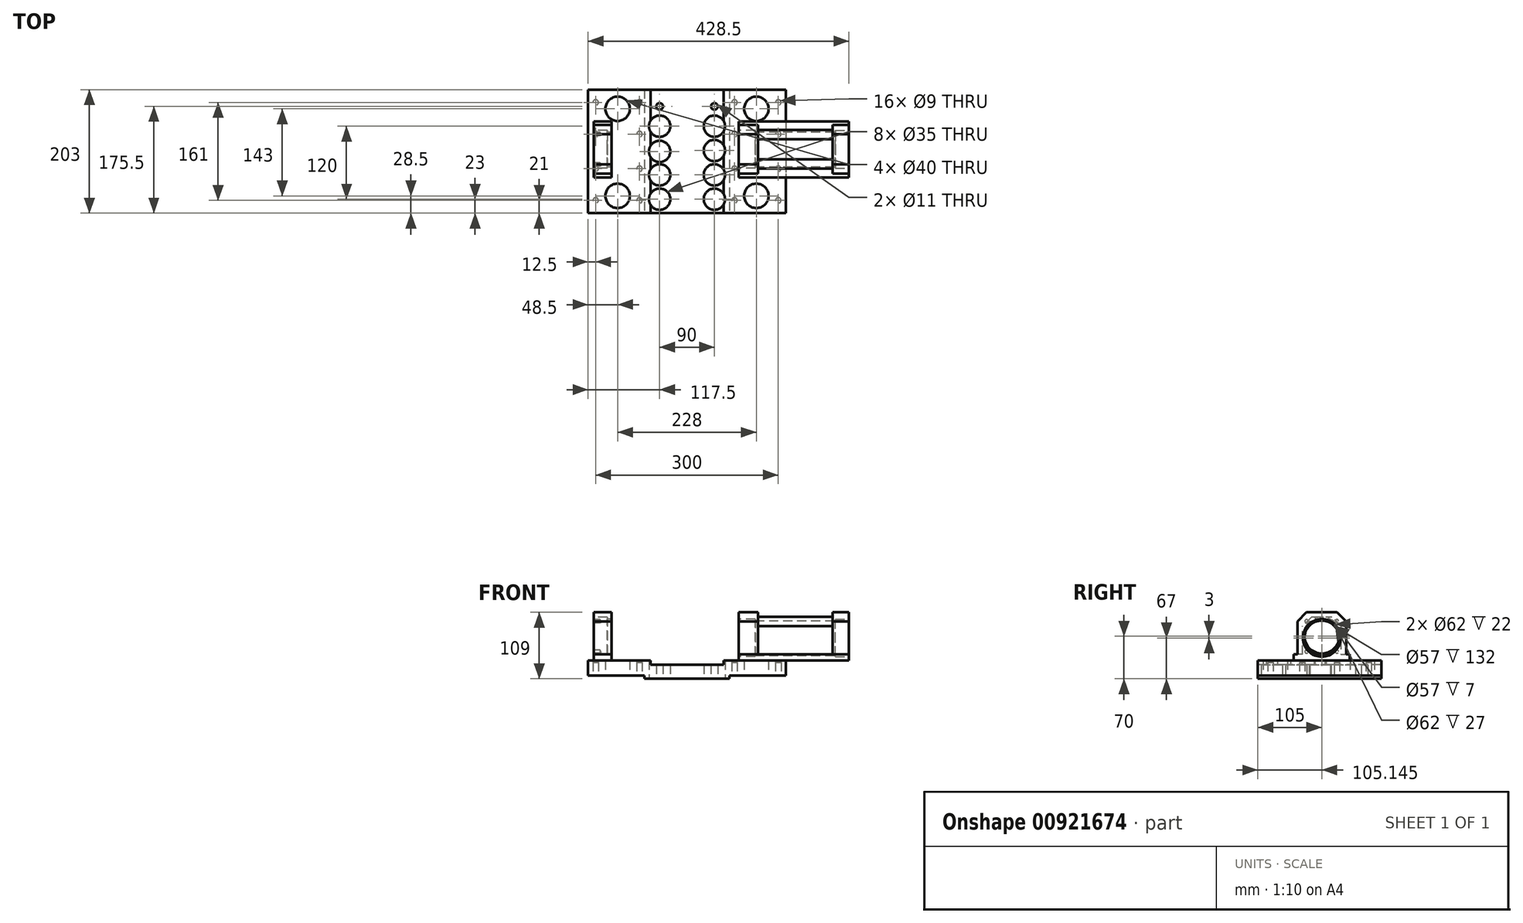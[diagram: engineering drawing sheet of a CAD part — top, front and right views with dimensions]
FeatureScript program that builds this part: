
annotation { "Feature Type Name" : "Feature", "Feature Type Description" : "" }
export const myFeature = defineFeature(function(context is Context, id is Id, definition is map)
    precondition{}
    {
        {
            var Q0;
            Q0=qCreatedBy(makeId("Front.planeOp"),FACE);
            var sketch = newSketch(context, id + "F0", { "sketchPlane" : qUnion([Q0])});
            skLineSegment(sketch, "E0", {"start": v(0, 0) * mm, "end": v(0, 25) * mm});
            skLineSegment(sketch, "E1", {"start": v(0, 25) * mm, "end": v(325, 25) * mm});
            skLineSegment(sketch, "E2", {"start": v(325, 25) * mm, "end": v(325, 0) * mm});
            skLineSegment(sketch, "E3", {"start": v(325, 0) * mm, "end": v(232.5, 0) * mm});
            skLineSegment(sketch, "E4", {"start": v(232.5, 0) * mm, "end": v(232.5, -5) * mm});
            skLineSegment(sketch, "E5", {"start": v(232.5, -5) * mm, "end": v(92.5, -5) * mm});
            skLineSegment(sketch, "E6", {"start": v(92.5, -5) * mm, "end": v(92.5, 0) * mm});
            skLineSegment(sketch, "E7", {"start": v(92.5, 0) * mm, "end": v(0, 0) * mm});
            skLineSegment(sketch, "E8", {"start": v(162.5, 25) * mm, "end": v(162.5, -5) * mm, "construction": true});
            skLineSegment(sketch, "E9", {"start": v(102.5, 25) * mm, "end": v(102.5, 18) * mm});
            skLineSegment(sketch, "E10", {"start": v(102.5, 18) * mm, "end": v(222.5, 18) * mm});
            skLineSegment(sketch, "E11", {"start": v(222.5, 18) * mm, "end": v(222.5, 25) * mm});
            skLineSegment(sketch, "E12", {"start": v(102.5, 25) * mm, "end": v(222.5, 25) * mm});
            skSolve(sketch);
        }
        {
            var Q0;
            {var subQ1=sQuery(id+"F0.wireOp",EDGE,"E0");Q0=makeQuery(id+"F0.imprint","IMPRINT",FACE,{"disambiguationData":[TD([[makeQuery(id+"F0.imprint","IMPRINT",EDGE,{"derivedFrom":subQ1}),-1.0]])]});}
            extrude(context, id + "F1", {"entities" : qUnion([Q0]), "oppositeDirection" : true, "depth" : 203 * mm, "offsetDistance" : 25 * mm});
        }
        {
            var Q0;
            Q0=qCreatedBy(makeId("Right.planeOp"),FACE);
            cPlane(context, id + "F2", {"entities" : qUnion([Q0]), "cplaneType" : CPlaneType.OFFSET, "offset" : 38.5 * mm, "width" : 150 * mm, "height" : 150 * mm});
        }
        {
            var Q0;
            Q0=qCreatedBy(id+"F2.planeOp",FACE);
            var sketch = newSketch(context, id + "F3", { "sketchPlane" : qUnion([Q0])});
            skLineSegment(sketch, "E13.0", {"start": v(203, 25) * mm, "end": v(0, 25) * mm});
            skPoint(sketch, "E14", {"position": v(105, 25) * mm});
            skLineSegment(sketch, "E15", {"start": v(105, 114.48) * mm, "end": v(105, -54.55) * mm, "construction": true});
            skLineSegment(sketch, "E16", {"start": v(59, 25) * mm, "end": v(59, 35) * mm});
            skLineSegment(sketch, "E17", {"start": v(59, 35) * mm, "end": v(65, 35) * mm});
            skLineSegment(sketch, "E18", {"start": v(65, 35) * mm, "end": v(65, 104) * mm});
            skLineSegment(sketch, "E19", {"start": v(65, 104) * mm, "end": v(145, 104) * mm});
            skLineSegment(sketch, "E20", {"start": v(145, 104) * mm, "end": v(145, 35) * mm});
            skLineSegment(sketch, "E21", {"start": v(145, 35) * mm, "end": v(151, 35) * mm});
            skLineSegment(sketch, "E22", {"start": v(151, 35) * mm, "end": v(151, 25) * mm});
            skLineSegment(sketch, "E23", {"start": v(151, 25) * mm, "end": v(59, 25) * mm});
            skLineSegment(sketch, "E24", {"start": v(65, 69.5) * mm, "end": v(145, 69.5) * mm, "construction": true});
            skSolve(sketch);
        }
        {
            var Q0;
            {var subQ0=sQuery(id+"F3.wireOp",EDGE,"E16");Q0=makeQuery(id+"F3.imprint","IMPRINT",FACE,{"disambiguationData":[TD([[makeQuery(id+"F3.imprint","IMPRINT",EDGE,{"derivedFrom":subQ0}),-1.0]])]});}
            extrude(context, id + "F4", {"entities" : qUnion([Q0]), "operationType" : NewBodyOperationType.ADD, "oppositeDirection" : true, "depth" : 29 * mm, "offsetDistance" : 25 * mm});
        }
        {
            var Q0;
            Q0=makeQuery(id+"F4.opExtrude","SWEPT_EDGE",EDGE,{"disambiguationData":[OSD([sQuery(id+"F3.wireOp",EDGE,"E18"),sQuery(id+"F3.wireOp",EDGE,"E19")])]});
            var Q1;
            Q1=makeQuery(id+"F4.opExtrude","SWEPT_EDGE",EDGE,{"disambiguationData":[OSD([sQuery(id+"F3.wireOp",EDGE,"E19"),sQuery(id+"F3.wireOp",EDGE,"E20")])]});
            chamfer(context, id + "F5", {"entities" : qUnion([Q0, Q1]), "width" : 15 * mm, "tangentPropagation" : true});
        }
        {
            var Q0;
            Q0=makeQuery(id+"F4.opExtrude","CAP_FACE",FACE,{"disambiguationData":[OSD([sQuery(id+"F3.wireOp",EDGE,"E13.0"),sQuery(id+"F3.wireOp",EDGE,"E16"),sQuery(id+"F3.wireOp",EDGE,"E17"),sQuery(id+"F3.wireOp",EDGE,"E18"),sQuery(id+"F3.wireOp",EDGE,"E19"),sQuery(id+"F3.wireOp",EDGE,"E20"),sQuery(id+"F3.wireOp",EDGE,"E21"),sQuery(id+"F3.wireOp",EDGE,"E22")])],"isStart":true});
            var sketch = newSketch(context, id + "F6", { "sketchPlane" : qUnion([Q0])});
            skPoint(sketch, "E25", {"position": v(105.15, 65) * mm});
            skCircle(sketch, "E26", {"center": v(105.15, 65) * mm, "radius": 28.5 * mm});
            skSolve(sketch);
        }
        {
            var Q0;
            Q0=makeQuery(id+"F6.imprint","IMPRINT",FACE,{"disambiguationData":[TD([[makeQuery(id+"F6.imprint","IMPRINT",EDGE,{"derivedFrom":sQuery(id+"F6.wireOp",EDGE,"E26")}),1.0]])]});
            extrude(context, id + "F7", {"entities" : qUnion([Q0]), "operationType" : NewBodyOperationType.REMOVE, "oppositeDirection" : true, "depth" : 7 * mm, "offsetDistance" : 25 * mm});
        }
        {
            var Q0;
            Q0=makeQuery(id+"F4.opExtrude","CAP_FACE",FACE,{"disambiguationData":[OSD([sQuery(id+"F3.wireOp",EDGE,"E13.0"),sQuery(id+"F3.wireOp",EDGE,"E16"),sQuery(id+"F3.wireOp",EDGE,"E17"),sQuery(id+"F3.wireOp",EDGE,"E18"),sQuery(id+"F3.wireOp",EDGE,"E19"),sQuery(id+"F3.wireOp",EDGE,"E20"),sQuery(id+"F3.wireOp",EDGE,"E21"),sQuery(id+"F3.wireOp",EDGE,"E22")])],"isStart":false});
            var sketch = newSketch(context, id + "F8", { "sketchPlane" : qUnion([Q0])});
            skLineSegment(sketch, "E27", {"start": v(-105, 104) * mm, "end": v(-105, 0) * mm, "construction": true});
            skPoint(sketch, "E27.endSnap0", {"position": v(-105, 25) * mm});
            skPoint(sketch, "E28", {"position": v(-105, 65) * mm});
            skCircle(sketch, "E29", {"center": v(-105, 65) * mm, "radius": 31 * mm});
            skSolve(sketch);
        }
        {
            var Q0;
            Q0=makeQuery(id+"F8.imprint","IMPRINT",FACE,{"disambiguationData":[TD([[makeQuery(id+"F8.imprint","IMPRINT",EDGE,{"derivedFrom":sQuery(id+"F8.wireOp",EDGE,"E29")}),1.0]])]});
            var Q1;
            Q1=sQuery(id+"F8.wireOp",EDGE,"E29");
            extrude(context, id + "F9", {"entities" : qUnion([Q0]), "operationType" : NewBodyOperationType.REMOVE, "surfaceEntities" : qUnion([Q1]), "oppositeDirection" : true, "depth" : 22 * mm, "offsetDistance" : 25 * mm});
        }
        {
            var Q0;
            Q0=qCreatedBy(makeId("Top.planeOp"),FACE);
            var sketch = newSketch(context, id + "F10", { "sketchPlane" : qUnion([Q0])});
            skLineSegment(sketch, "E30.0", {"start": v(0, 203) * mm, "end": v(102.5, 203) * mm, "construction": true});
            skLineSegment(sketch, "E31", {"start": v(48.5, 203) * mm, "end": v(48.5, 0) * mm, "construction": true});
            skLineSegment(sketch, "E32", {"start": v(84.5, 203) * mm, "end": v(84.5, 0) * mm, "construction": true});
            skLineSegment(sketch, "E33.0", {"start": v(102.5, 203) * mm, "end": v(222.5, 203) * mm});
            skLineSegment(sketch, "E34", {"start": v(162.5, 203) * mm, "end": v(162.5, 0) * mm, "construction": true});
            skLineSegment(sketch, "E35", {"start": v(117.5, 203) * mm, "end": v(117.5, 0) * mm, "construction": true});
            skLineSegment(sketch, "E36", {"start": v(207.5, 203) * mm, "end": v(207.5, 0) * mm, "construction": true});
            skLineSegment(sketch, "E37.0", {"start": v(222.5, 203) * mm, "end": v(325, 203) * mm, "construction": true});
            skLineSegment(sketch, "E38", {"start": v(240.5, 203) * mm, "end": v(240.5, 0) * mm, "construction": true});
            skLineSegment(sketch, "E39", {"start": v(276.5, 203) * mm, "end": v(276.5, 0) * mm, "construction": true});
            skLineSegment(sketch, "E40", {"start": v(12.5, 203) * mm, "end": v(12.5, 0) * mm, "construction": true});
            skLineSegment(sketch, "E41", {"start": v(312.5, 203) * mm, "end": v(312.5, 0) * mm, "construction": true});
            skPoint(sketch, "E42", {"position": v(12.5, 182) * mm});
            skPoint(sketch, "E43", {"position": v(12.5, 130) * mm});
            skPoint(sketch, "E44", {"position": v(12.5, 73) * mm});
            skPoint(sketch, "E45", {"position": v(12.5, 21) * mm});
            skPoint(sketch, "E46", {"position": v(48.5, 171.5) * mm});
            skPoint(sketch, "E47", {"position": v(48.5, 28.5) * mm});
            skPoint(sketch, "E48", {"position": v(84.5, 182) * mm});
            skPoint(sketch, "E49", {"position": v(84.5, 130) * mm});
            skPoint(sketch, "E50", {"position": v(84.5, 73) * mm});
            skPoint(sketch, "E51", {"position": v(84.5, 21) * mm});
            skPoint(sketch, "E52", {"position": v(117.5, 175.5) * mm});
            skPoint(sketch, "E53", {"position": v(207.5, 175.5) * mm});
            skPoint(sketch, "E54", {"position": v(117.5, 143) * mm});
            skPoint(sketch, "E55", {"position": v(117.5, 103) * mm});
            skPoint(sketch, "E56", {"position": v(117.5, 63) * mm});
            skPoint(sketch, "E57", {"position": v(117.5, 23) * mm});
            skPoint(sketch, "E58", {"position": v(207.5, 143) * mm});
            skPoint(sketch, "E59", {"position": v(207.5, 103) * mm});
            skPoint(sketch, "E60", {"position": v(207.5, 63) * mm});
            skPoint(sketch, "E61", {"position": v(207.5, 23) * mm});
            skPoint(sketch, "E62", {"position": v(240.5, 182) * mm});
            skPoint(sketch, "E63", {"position": v(240.5, 130) * mm});
            skPoint(sketch, "E64", {"position": v(240.5, 73) * mm});
            skPoint(sketch, "E65", {"position": v(240.5, 21) * mm});
            skPoint(sketch, "E66", {"position": v(312.5, 21) * mm});
            skPoint(sketch, "E67", {"position": v(312.5, 73) * mm});
            skPoint(sketch, "E68", {"position": v(312.5, 130) * mm});
            skPoint(sketch, "E69", {"position": v(312.5, 182) * mm});
            skPoint(sketch, "E70", {"position": v(276.5, 171.5) * mm});
            skPoint(sketch, "E71", {"position": v(276.5, 28.5) * mm});
            skLineSegment(sketch, "E72.0", {"start": v(0, 203) * mm, "end": v(0, 0) * mm, "construction": true});
            skPoint(sketch, "E73", {"position": v(0, 101.5) * mm});
            skLineSegment(sketch, "E74", {"start": v(0, 101.5) * mm, "end": v(351.57, 101.5) * mm, "construction": true});
            skLineSegment(sketch, "E75.0", {"start": v(102.5, 203) * mm, "end": v(102.5, 0) * mm});
            skLineSegment(sketch, "E76.0", {"start": v(222.5, 203) * mm, "end": v(222.5, 0) * mm});
            skLineSegment(sketch, "E77", {"start": v(102.5, 148) * mm, "end": v(222.5, 148) * mm});
            skSolve(sketch);
        }
        {
            var Q0;
            Q0=sQuery(id+"F10.wireOp",VERTEX,"E42");
            var Q1;
            Q1=sQuery(id+"F10.wireOp",VERTEX,"E43");
            var Q2;
            Q2=sQuery(id+"F10.wireOp",VERTEX,"E44");
            var Q3;
            Q3=sQuery(id+"F10.wireOp",VERTEX,"E45");
            var Q4;
            Q4=sQuery(id+"F10.wireOp",VERTEX,"E50");
            var Q5;
            Q5=sQuery(id+"F10.wireOp",VERTEX,"E49");
            var Q6;
            Q6=sQuery(id+"F10.wireOp",VERTEX,"E48");
            var Q7;
            Q7=sQuery(id+"F10.wireOp",VERTEX,"E62");
            var Q8;
            Q8=sQuery(id+"F10.wireOp",VERTEX,"E69");
            var Q9;
            Q9=sQuery(id+"F10.wireOp",VERTEX,"E63");
            var Q10;
            Q10=sQuery(id+"F10.wireOp",VERTEX,"E68");
            var Q11;
            Q11=sQuery(id+"F10.wireOp",VERTEX,"E64");
            var Q12;
            Q12=sQuery(id+"F10.wireOp",VERTEX,"E67");
            var Q13;
            Q13=sQuery(id+"F10.wireOp",VERTEX,"E65");
            var Q14;
            Q14=sQuery(id+"F10.wireOp",VERTEX,"E66");
            var Q15;
            Q15=sQuery(id+"F10.wireOp",VERTEX,"E51");
            var Q16;
            Q16=makeQuery(id+"F1.opExtrude","SWEPT_BODY",BODY,{"disambiguationData":[OSD([sQuery(id+"F0.wireOp",EDGE,"E0"),sQuery(id+"F0.wireOp",EDGE,"E1"),sQuery(id+"F0.wireOp",EDGE,"E2"),sQuery(id+"F0.wireOp",EDGE,"E3"),sQuery(id+"F0.wireOp",EDGE,"E4"),sQuery(id+"F0.wireOp",EDGE,"E5"),sQuery(id+"F0.wireOp",EDGE,"E6"),sQuery(id+"F0.wireOp",EDGE,"E7"),sQuery(id+"F0.wireOp",EDGE,"E9"),sQuery(id+"F0.wireOp",EDGE,"E10"),sQuery(id+"F0.wireOp",EDGE,"E11")])]});
            hole(context, id + "F11", {"style" : HoleStyle.SIMPLE, "endStyle" : HoleEndStyle.BLIND, "oppositeDirection" : true, "standardTappedOrClearance" : lookupTablePath({ "fit" : "Normal", "standard" : "ISO", "size" : "M8", "type" : "Clearance" }), "standardBlindInLast" : lookupTablePath({ "fit" : "Normal", "standard" : "ISO", "size" : "M8", "type" : "Clearance" }), "holeDiameter" : 9 * mm, "majorDiameter" : 5 * mm, "holeDepth" : 22 * mm, "isTappedThrough" : true, "tappedDepth" : 12 * mm, "tapClearance" : 3, "locations" : qUnion([Q0, Q1, Q2, Q3, Q4, Q5, Q6, Q7, Q8, Q9, Q10, Q11, Q12, Q13, Q14, Q15]), "scope" : qUnion([Q16])});
        }
        {
            var Q0;
            Q0=sQuery(id+"F10.wireOp",VERTEX,"E47");
            var Q1;
            Q1=sQuery(id+"F10.wireOp",VERTEX,"E46");
            var Q2;
            Q2=sQuery(id+"F10.wireOp",VERTEX,"E71");
            var Q3;
            Q3=sQuery(id+"F10.wireOp",VERTEX,"E70");
            var Q4;
            Q4=makeQuery(id+"F1.opExtrude","SWEPT_BODY",BODY,{"disambiguationData":[OSD([sQuery(id+"F0.wireOp",EDGE,"E0"),sQuery(id+"F0.wireOp",EDGE,"E1"),sQuery(id+"F0.wireOp",EDGE,"E2"),sQuery(id+"F0.wireOp",EDGE,"E3"),sQuery(id+"F0.wireOp",EDGE,"E4"),sQuery(id+"F0.wireOp",EDGE,"E5"),sQuery(id+"F0.wireOp",EDGE,"E6"),sQuery(id+"F0.wireOp",EDGE,"E7"),sQuery(id+"F0.wireOp",EDGE,"E9"),sQuery(id+"F0.wireOp",EDGE,"E10"),sQuery(id+"F0.wireOp",EDGE,"E11")])]});
            hole(context, id + "F12", {"style" : HoleStyle.SIMPLE, "endStyle" : HoleEndStyle.THROUGH, "oppositeDirection" : true, "holeDiameter" : 40 * mm, "majorDiameter" : 5 * mm, "isTappedThrough" : true, "tappedDepth" : 12 * mm, "tapClearance" : 3, "locations" : qUnion([Q0, Q1, Q2, Q3]), "scope" : qUnion([Q4])});
        }
        {
            var Q0;
            Q0=makeQuery(id+"F1.opExtrude","SWEPT_FACE",FACE,{"disambiguationData":[OSD([sQuery(id+"F0.wireOp",EDGE,"E5")])]});
            var sketch = newSketch(context, id + "F13", { "sketchPlane" : qUnion([Q0])});
            skPoint(sketch, "E78.0", {"position": v(117.5, -23) * mm});
            skPoint(sketch, "E79.0", {"position": v(207.5, -23) * mm});
            skPoint(sketch, "E80.0", {"position": v(117.5, -63) * mm});
            skPoint(sketch, "E81.0", {"position": v(207.5, -63) * mm});
            skPoint(sketch, "E82.0", {"position": v(117.5, -101.5) * mm});
            skPoint(sketch, "E83.0", {"position": v(207.5, -103) * mm});
            skPoint(sketch, "E84.0", {"position": v(117.5, -143) * mm});
            skPoint(sketch, "E85.0", {"position": v(117.5, -175.5) * mm});
            skPoint(sketch, "E86.0", {"position": v(207.5, -143) * mm});
            skPoint(sketch, "E87.0", {"position": v(207.5, -175.5) * mm});
            skSolve(sketch);
        }
        {
            var Q0;
            Q0=sQuery(id+"F13.wireOp",VERTEX,"E78.0");
            var Q1;
            Q1=sQuery(id+"F13.wireOp",VERTEX,"E80.0");
            var Q2;
            Q2=sQuery(id+"F13.wireOp",VERTEX,"E84.0");
            var Q3;
            Q3=sQuery(id+"F13.wireOp",VERTEX,"E86.0");
            var Q4;
            Q4=sQuery(id+"F13.wireOp",VERTEX,"E83.0");
            var Q5;
            Q5=sQuery(id+"F13.wireOp",VERTEX,"E82.0");
            var Q6;
            Q6=sQuery(id+"F13.wireOp",VERTEX,"E81.0");
            var Q7;
            Q7=sQuery(id+"F13.wireOp",VERTEX,"E79.0");
            var Q8;
            Q8=makeQuery(id+"F1.opExtrude","SWEPT_BODY",BODY,{"disambiguationData":[OSD([sQuery(id+"F0.wireOp",EDGE,"E0"),sQuery(id+"F0.wireOp",EDGE,"E1"),sQuery(id+"F0.wireOp",EDGE,"E2"),sQuery(id+"F0.wireOp",EDGE,"E3"),sQuery(id+"F0.wireOp",EDGE,"E4"),sQuery(id+"F0.wireOp",EDGE,"E5"),sQuery(id+"F0.wireOp",EDGE,"E6"),sQuery(id+"F0.wireOp",EDGE,"E7"),sQuery(id+"F0.wireOp",EDGE,"E9"),sQuery(id+"F0.wireOp",EDGE,"E10"),sQuery(id+"F0.wireOp",EDGE,"E11")])]});
            hole(context, id + "F14", {"style" : HoleStyle.SIMPLE, "endStyle" : HoleEndStyle.THROUGH, "holeDiameter" : 35 * mm, "majorDiameter" : 5 * mm, "isTappedThrough" : true, "tappedDepth" : 12 * mm, "tapClearance" : 3, "locations" : qUnion([Q0, Q1, Q2, Q3, Q4, Q5, Q6, Q7]), "scope" : qUnion([Q8])});
        }
        {
            var Q0;
            Q0=sQuery(id+"F13.wireOp",VERTEX,"E85.0");
            var Q1;
            Q1=sQuery(id+"F13.wireOp",VERTEX,"E87.0");
            var Q2;
            Q2=makeQuery(id+"F1.opExtrude","SWEPT_BODY",BODY,{"disambiguationData":[OSD([sQuery(id+"F0.wireOp",EDGE,"E0"),sQuery(id+"F0.wireOp",EDGE,"E1"),sQuery(id+"F0.wireOp",EDGE,"E2"),sQuery(id+"F0.wireOp",EDGE,"E3"),sQuery(id+"F0.wireOp",EDGE,"E4"),sQuery(id+"F0.wireOp",EDGE,"E5"),sQuery(id+"F0.wireOp",EDGE,"E6"),sQuery(id+"F0.wireOp",EDGE,"E7"),sQuery(id+"F0.wireOp",EDGE,"E9"),sQuery(id+"F0.wireOp",EDGE,"E10"),sQuery(id+"F0.wireOp",EDGE,"E11")])]});
            hole(context, id + "F15", {"style" : HoleStyle.SIMPLE, "endStyle" : HoleEndStyle.THROUGH, "standardTappedOrClearance" : lookupTablePath({ "fit" : "Normal", "standard" : "ISO", "size" : "M10", "type" : "Clearance" }), "standardBlindInLast" : lookupTablePath({ "fit" : "Normal", "standard" : "ISO", "size" : "M10", "type" : "Clearance" }), "holeDiameter" : 11 * mm, "majorDiameter" : 5 * mm, "isTappedThrough" : true, "tappedDepth" : 12 * mm, "tapClearance" : 3, "locations" : qUnion([Q0, Q1]), "scope" : qUnion([Q2])});
        }
        {
            var Q0;
            Q0=qCreatedBy(id+"F2.planeOp",FACE);
            cPlane(context, id + "F16", {"entities" : qUnion([Q0]), "cplaneType" : CPlaneType.OFFSET, "offset" : 209 * mm, "width" : 150 * mm, "height" : 150 * mm});
        }
        {
            var Q0;
            Q0=qCreatedBy(id+"F16.planeOp",FACE);
            var sketch = newSketch(context, id + "F17", { "sketchPlane" : qUnion([Q0])});
            skLineSegment(sketch, "E88.0", {"start": v(203, 25) * mm, "end": v(0, 25) * mm});
            skPoint(sketch, "E89", {"position": v(101.5, 25) * mm});
            skSolve(sketch);
        }
        {
            var Q0;
            Q0=qCreatedBy(id+"F16.planeOp",FACE);
            var sketch = newSketch(context, id + "F18", { "sketchPlane" : qUnion([Q0])});
            skLineSegment(sketch, "E90.0", {"start": v(203, 25) * mm, "end": v(0, 25) * mm});
            skPoint(sketch, "E91", {"position": v(105, 25) * mm});
            skLineSegment(sketch, "E92", {"start": v(105, 110.25) * mm, "end": v(105, -70.77) * mm, "construction": true});
            skLineSegment(sketch, "E93", {"start": v(59, 25) * mm, "end": v(59, 35) * mm});
            skLineSegment(sketch, "E94", {"start": v(59, 35) * mm, "end": v(65, 35) * mm});
            skLineSegment(sketch, "E95", {"start": v(65, 35) * mm, "end": v(65, 104) * mm});
            skLineSegment(sketch, "E96", {"start": v(65, 104) * mm, "end": v(145, 104) * mm});
            skLineSegment(sketch, "E97", {"start": v(145, 104) * mm, "end": v(145, 35) * mm});
            skLineSegment(sketch, "E98", {"start": v(145, 35) * mm, "end": v(151, 35) * mm});
            skLineSegment(sketch, "E99", {"start": v(151, 35) * mm, "end": v(151, 25) * mm});
            skLineSegment(sketch, "E100", {"start": v(151, 25) * mm, "end": v(59, 25) * mm});
            skCircle(sketch, "E101.0", {"center": v(105.15, 65) * mm, "radius": 28.5 * mm});
            skCircle(sketch, "E102", {"center": v(105.15, 65) * mm, "radius": 31 * mm});
            skSolve(sketch);
        }
        {
            var Q0;
            {var subQ0=sQuery(id+"F18.wireOp",EDGE,"E93");Q0=makeQuery(id+"F18.imprint","IMPRINT",FACE,{"disambiguationData":[TD([[makeQuery(id+"F18.imprint","IMPRINT",EDGE,{"derivedFrom":subQ0}),-1.0]])]});}
            extrude(context, id + "F19", {"entities" : qUnion([Q0]), "operationType" : NewBodyOperationType.ADD, "depth" : 32 * mm, "offsetDistance" : 25 * mm});
        }
        {
            var Q0;
            Q0=makeQuery(id+"F19.opExtrude","SWEPT_EDGE",EDGE,{"disambiguationData":[OSD([sQuery(id+"F18.wireOp",EDGE,"E95"),sQuery(id+"F18.wireOp",EDGE,"E96")])]});
            var Q1;
            Q1=makeQuery(id+"F19.opExtrude","SWEPT_EDGE",EDGE,{"disambiguationData":[OSD([sQuery(id+"F18.wireOp",EDGE,"E96"),sQuery(id+"F18.wireOp",EDGE,"E97")])]});
            chamfer(context, id + "F20", {"entities" : qUnion([Q0, Q1]), "width" : 15 * mm, "tangentPropagation" : true});
        }
        {
            var Q0;
            Q0=makeQuery(id+"F19.opExtrude","CAP_FACE",FACE,{"disambiguationData":[OSD([sQuery(id+"F18.wireOp",EDGE,"E90.0"),sQuery(id+"F18.wireOp",EDGE,"E93"),sQuery(id+"F18.wireOp",EDGE,"E94"),sQuery(id+"F18.wireOp",EDGE,"E95"),sQuery(id+"F18.wireOp",EDGE,"E96"),sQuery(id+"F18.wireOp",EDGE,"E97"),sQuery(id+"F18.wireOp",EDGE,"E98"),sQuery(id+"F18.wireOp",EDGE,"E99"),sQuery(id+"F18.wireOp",EDGE,"E102")])],"isStart":false});
            var sketch = newSketch(context, id + "F21", { "sketchPlane" : qUnion([Q0])});
            skLineSegment(sketch, "E103", {"start": v(145, 35) * mm, "end": v(136.5, 35) * mm});
            skLineSegment(sketch, "E104", {"start": v(105, 104) * mm, "end": v(105, 25) * mm, "construction": true});
            skLineSegment(sketch, "E105", {"start": v(73.5, 35) * mm, "end": v(73.5, 96.5) * mm});
            skLineSegment(sketch, "E106", {"start": v(73.5, 96.5) * mm, "end": v(136.5, 96.5) * mm});
            skLineSegment(sketch, "E107", {"start": v(73.5, 35) * mm, "end": v(59, 35) * mm});
            skLineSegment(sketch, "E108", {"start": v(59, 35) * mm, "end": v(59, 25) * mm});
            skLineSegment(sketch, "E109", {"start": v(59, 25) * mm, "end": v(151, 25) * mm});
            skLineSegment(sketch, "E110", {"start": v(151, 25) * mm, "end": v(151, 35) * mm});
            skLineSegment(sketch, "E111", {"start": v(136.5, 96.5) * mm, "end": v(136.5, 35) * mm});
            skLineSegment(sketch, "E112", {"start": v(136.5, 35) * mm, "end": v(151, 35) * mm});
            skLineSegment(sketch, "E113.trimOffspring", {"start": v(73.5, 35) * mm, "end": v(65, 35) * mm});
            skSolve(sketch);
        }
        {
            var Q0;
            Q0=makeQuery(id+"F21.imprint","IMPRINT",FACE,{"disambiguationData":[TD([[makeQuery(id+"F21.imprint","IMPRINT",EDGE,{"derivedFrom":sQuery(id+"F21.wireOp",EDGE,"E105")}),-1.0]])]});
            extrude(context, id + "F22", {"entities" : qUnion([Q0]), "operationType" : NewBodyOperationType.ADD, "depth" : 122 * mm, "offsetDistance" : 25 * mm});
        }
        {
            var Q0;
            Q0=makeQuery(id+"F22.opExtrude","SWEPT_EDGE",EDGE,{"disambiguationData":[OSD([sQuery(id+"F21.wireOp",EDGE,"E105"),sQuery(id+"F21.wireOp",EDGE,"E106")])]});
            var Q1;
            Q1=makeQuery(id+"F22.opExtrude","SWEPT_EDGE",EDGE,{"disambiguationData":[OSD([sQuery(id+"F21.wireOp",EDGE,"E106"),sQuery(id+"F21.wireOp",EDGE,"E111")])]});
            chamfer(context, id + "F23", {"entities" : qUnion([Q0, Q1]), "width" : 15 * mm, "tangentPropagation" : true});
        }
        {
            var Q0;
            Q0=makeQuery(id+"F22.opExtrude","CAP_FACE",FACE,{"disambiguationData":[OSD([sQuery(id+"F21.wireOp",EDGE,"E105"),sQuery(id+"F21.wireOp",EDGE,"E106"),sQuery(id+"F21.wireOp",EDGE,"E107"),sQuery(id+"F21.wireOp",EDGE,"E108"),sQuery(id+"F21.wireOp",EDGE,"E109"),sQuery(id+"F21.wireOp",EDGE,"E110"),sQuery(id+"F21.wireOp",EDGE,"E111"),sQuery(id+"F21.wireOp",EDGE,"E112"),sQuery(id+"F21.wireOp",EDGE,"E113.trimOffspring")])],"isStart":false});
            var sketch = newSketch(context, id + "F24", { "sketchPlane" : qUnion([Q0])});
            skLineSegment(sketch, "E114", {"start": v(59, 25) * mm, "end": v(59, 35) * mm});
            skLineSegment(sketch, "E115", {"start": v(59, 35) * mm, "end": v(65, 35) * mm});
            skLineSegment(sketch, "E116", {"start": v(65, 35) * mm, "end": v(65, 104) * mm});
            skLineSegment(sketch, "E117", {"start": v(65, 104) * mm, "end": v(145, 104) * mm});
            skLineSegment(sketch, "E118", {"start": v(145, 104) * mm, "end": v(145, 35) * mm});
            skLineSegment(sketch, "E119", {"start": v(145, 35) * mm, "end": v(151, 35) * mm});
            skLineSegment(sketch, "E120", {"start": v(151, 35) * mm, "end": v(151, 25) * mm});
            skLineSegment(sketch, "E121", {"start": v(151, 25) * mm, "end": v(59, 25) * mm});
            skLineSegment(sketch, "E122", {"start": v(105, 104) * mm, "end": v(105, 25) * mm, "construction": true});
            skSolve(sketch);
        }
        {
            var Q0;
            {var subQ6=sQuery(id+"F24.wireOp",EDGE,"E116");Q0=makeQuery(id+"F24.imprint","IMPRINT",FACE,{"disambiguationData":[TD([[makeQuery(id+"F24.imprint","IMPRINT",EDGE,{"derivedFrom":subQ6}),-1.0]])]});}
            var Q1;
            Q1=makeQuery(id+"F24.imprint","IMPRINT",FACE,{"disambiguationData":[TD([[makeQuery(id+"F24.imprint","IMPRINT",EDGE,{"derivedFrom":sQuery(id+"F24.wireOp",EDGE,"E114")}),-1.0]])]});
            extrude(context, id + "F25", {"entities" : qUnion([Q0, Q1]), "operationType" : NewBodyOperationType.ADD, "depth" : 27 * mm, "offsetDistance" : 25 * mm});
        }
        {
            var Q0;
            Q0=makeQuery(id+"F25.opExtrude","SWEPT_EDGE",EDGE,{"disambiguationData":[OSD([sQuery(id+"F24.wireOp",EDGE,"E116"),sQuery(id+"F24.wireOp",EDGE,"E117")])]});
            var Q1;
            Q1=makeQuery(id+"F25.opExtrude","SWEPT_EDGE",EDGE,{"disambiguationData":[OSD([sQuery(id+"F24.wireOp",EDGE,"E117"),sQuery(id+"F24.wireOp",EDGE,"E118")])]});
            chamfer(context, id + "F26", {"entities" : qUnion([Q0, Q1]), "width" : 15 * mm, "tangentPropagation" : true});
        }
        {
            var Q0;
            Q0=makeQuery(id+"F4.opExtrude","CAP_FACE",FACE,{"disambiguationData":[OSD([sQuery(id+"F3.wireOp",EDGE,"E13.0"),sQuery(id+"F3.wireOp",EDGE,"E16"),sQuery(id+"F3.wireOp",EDGE,"E17"),sQuery(id+"F3.wireOp",EDGE,"E18"),sQuery(id+"F3.wireOp",EDGE,"E19"),sQuery(id+"F3.wireOp",EDGE,"E20"),sQuery(id+"F3.wireOp",EDGE,"E21"),sQuery(id+"F3.wireOp",EDGE,"E22")])],"isStart":false});
            var sketch = newSketch(context, id + "F27", { "sketchPlane" : qUnion([Q0])});
            skLineSegment(sketch, "E123", {"start": v(-105, 104) * mm, "end": v(-105, 25) * mm, "construction": true});
            skLineSegment(sketch, "E124", {"start": v(-130, 104) * mm, "end": v(-130, 25) * mm, "construction": true});
            skLineSegment(sketch, "E125", {"start": v(-80, 104) * mm, "end": v(-80, 25) * mm, "construction": true});
            skLineSegment(sketch, "E126", {"start": v(-153, 64.5) * mm, "end": v(-28.17, 64.5) * mm, "construction": true});
            skPoint(sketch, "E126.startSnap0", {"position": v(-105, 64.5) * mm});
            skLineSegment(sketch, "E127", {"start": v(-105, 64.5) * mm, "end": v(-167.48, 126.98) * mm, "construction": true});
            skLineSegment(sketch, "E128", {"start": v(-105, 64.5) * mm, "end": v(-30.88, 138.62) * mm, "construction": true});
            skLineSegment(sketch, "E129", {"start": v(-105, 64.5) * mm, "end": v(-166, 3.5) * mm, "construction": true});
            skLineSegment(sketch, "E130", {"start": v(-105, 64.5) * mm, "end": v(-46.74, 6.24) * mm, "construction": true});
            skPoint(sketch, "E131", {"position": v(-130, 89.5) * mm});
            skPoint(sketch, "E132", {"position": v(-80, 89.5) * mm});
            skPoint(sketch, "E133", {"position": v(-130, 39.5) * mm});
            skPoint(sketch, "E134", {"position": v(-80, 39.5) * mm});
            skSolve(sketch);
        }
        {
            var Q0;
            Q0=sQuery(id+"F27.wireOp",VERTEX,"E131");
            var Q1;
            Q1=sQuery(id+"F27.wireOp",VERTEX,"E132");
            var Q2;
            Q2=sQuery(id+"F27.wireOp",VERTEX,"E133");
            var Q3;
            Q3=sQuery(id+"F27.wireOp",VERTEX,"E134");
            var Q4;
            Q4=makeQuery(id+"F1.opExtrude","SWEPT_BODY",BODY,{"disambiguationData":[OSD([sQuery(id+"F0.wireOp",EDGE,"E0"),sQuery(id+"F0.wireOp",EDGE,"E1"),sQuery(id+"F0.wireOp",EDGE,"E2"),sQuery(id+"F0.wireOp",EDGE,"E3"),sQuery(id+"F0.wireOp",EDGE,"E4"),sQuery(id+"F0.wireOp",EDGE,"E5"),sQuery(id+"F0.wireOp",EDGE,"E6"),sQuery(id+"F0.wireOp",EDGE,"E7"),sQuery(id+"F0.wireOp",EDGE,"E9"),sQuery(id+"F0.wireOp",EDGE,"E10"),sQuery(id+"F0.wireOp",EDGE,"E11")])]});
            hole(context, id + "F28", {"style" : HoleStyle.SIMPLE, "endStyle" : HoleEndStyle.BLIND, "standardTappedOrClearance" : lookupTablePath({ "fit" : "Normal", "standard" : "ISO", "size" : "M5", "type" : "Clearance" }), "standardBlindInLast" : lookupTablePath({ "fit" : "Normal", "standard" : "ISO", "size" : "M5", "type" : "Clearance" }), "holeDiameter" : 5.5 * mm, "majorDiameter" : 5 * mm, "holeDepth" : 10 * mm, "isTappedThrough" : true, "tappedDepth" : 12 * mm, "tapClearance" : 3, "locations" : qUnion([Q0, Q1, Q2, Q3]), "scope" : qUnion([Q4])});
        }
        {
            var Q0;
            Q0=makeQuery(id+"F25.opExtrude","CAP_FACE",FACE,{"disambiguationData":[OSD([sQuery(id+"F18.wireOp",EDGE,"E102"),sQuery(id+"F24.wireOp",EDGE,"E114"),sQuery(id+"F24.wireOp",EDGE,"E115"),sQuery(id+"F24.wireOp",EDGE,"E116"),sQuery(id+"F24.wireOp",EDGE,"E117"),sQuery(id+"F24.wireOp",EDGE,"E118"),sQuery(id+"F24.wireOp",EDGE,"E119"),sQuery(id+"F24.wireOp",EDGE,"E120"),sQuery(id+"F24.wireOp",EDGE,"E121")])],"isStart":false});
            var sketch = newSketch(context, id + "F29", { "sketchPlane" : qUnion([Q0])});
            skPoint(sketch, "E135", {"position": v(105.15, 65) * mm});
            skCircle(sketch, "E136", {"center": v(105.15, 65) * mm, "radius": 31 * mm});
            skSolve(sketch);
        }
        {
            var Q0;
            Q0=makeQuery(id+"F29.imprint","IMPRINT",FACE,{"disambiguationData":[TD([[makeQuery(id+"F29.imprint","IMPRINT",EDGE,{"derivedFrom":sQuery(id+"F29.wireOp",EDGE,"E136")}),1.0]])]});
            extrude(context, id + "F30", {"entities" : qUnion([Q0]), "operationType" : NewBodyOperationType.ADD, "oppositeDirection" : true, "depth" : 181 * mm, "offsetDistance" : 25 * mm});
        }
        {
            var Q0;
            Q0=makeQuery(id+"F30.boolean.opBoolean","MERGE",FACE,{"derivedFrom":[makeQuery(id+"F19.opExtrude","CAP_FACE",FACE,{"disambiguationData":[OSD([sQuery(id+"F18.wireOp",EDGE,"E90.0"),sQuery(id+"F18.wireOp",EDGE,"E93"),sQuery(id+"F18.wireOp",EDGE,"E94"),sQuery(id+"F18.wireOp",EDGE,"E95"),sQuery(id+"F18.wireOp",EDGE,"E96"),sQuery(id+"F18.wireOp",EDGE,"E97"),sQuery(id+"F18.wireOp",EDGE,"E98"),sQuery(id+"F18.wireOp",EDGE,"E99"),sQuery(id+"F18.wireOp",EDGE,"E102")])],"isStart":true}),makeQuery(id+"F30.opExtrude","CAP_FACE",FACE,{"disambiguationData":[OSD([sQuery(id+"F29.wireOp",EDGE,"E136")])],"isStart":false})]});
            var sketch = newSketch(context, id + "F31", { "sketchPlane" : qUnion([Q0])});
            skPoint(sketch, "E137", {"position": v(-105, 62) * mm});
            skPoint(sketch, "E137.positionSnap0", {"position": v(-145, 62) * mm});
            skPoint(sketch, "E137.positionSnap1", {"position": v(-105, 104) * mm});
            skCircle(sketch, "E138", {"center": v(-105, 62) * mm, "radius": 31 * mm});
            skSolve(sketch);
        }
        {
            var Q0;
            Q0=makeQuery(id+"F31.imprint","IMPRINT",FACE,{"disambiguationData":[TD([[makeQuery(id+"F31.imprint","IMPRINT",EDGE,{"derivedFrom":sQuery(id+"F31.wireOp",EDGE,"E138")}),1.0]])]});
            extrude(context, id + "F32", {"entities" : qUnion([Q0]), "operationType" : NewBodyOperationType.ADD, "oppositeDirection" : true, "depth" : 5 * mm, "offsetDistance" : 25 * mm});
        }
        {
            var Q0;
            Q0=makeQuery(id+"F31.imprint","IMPRINT",FACE,{"disambiguationData":[TD([[makeQuery(id+"F31.imprint","IMPRINT",EDGE,{"derivedFrom":sQuery(id+"F31.wireOp",EDGE,"E138")}),1.0]])]});
            extrude(context, id + "F33", {"entities" : qUnion([Q0]), "operationType" : NewBodyOperationType.REMOVE, "oppositeDirection" : true, "depth" : 27 * mm, "offsetDistance" : 25 * mm});
        }
        {
            var Q0;
            Q0=makeQuery(id+"F30.boolean.opBoolean","MERGE",FACE,{"derivedFrom":[makeQuery(id+"F25.opExtrude","CAP_FACE",FACE,{"disambiguationData":[OSD([sQuery(id+"F18.wireOp",EDGE,"E102"),sQuery(id+"F24.wireOp",EDGE,"E114"),sQuery(id+"F24.wireOp",EDGE,"E115"),sQuery(id+"F24.wireOp",EDGE,"E116"),sQuery(id+"F24.wireOp",EDGE,"E117"),sQuery(id+"F24.wireOp",EDGE,"E118"),sQuery(id+"F24.wireOp",EDGE,"E119"),sQuery(id+"F24.wireOp",EDGE,"E120"),sQuery(id+"F24.wireOp",EDGE,"E121")])],"isStart":false}),makeQuery(id+"F30.opExtrude","CAP_FACE",FACE,{"disambiguationData":[OSD([sQuery(id+"F29.wireOp",EDGE,"E136")])],"isStart":true})]});
            var sketch = newSketch(context, id + "F34", { "sketchPlane" : qUnion([Q0])});
            skCircle(sketch, "E139", {"center": v(105, 62) * mm, "radius": 28.5 * mm});
            skPoint(sketch, "E139.centerSnap0", {"position": v(65, 62) * mm});
            skPoint(sketch, "E139.centerSnap1", {"position": v(105, 104) * mm});
            skSolve(sketch);
        }
        {
            var Q0;
            Q0=makeQuery(id+"F34.imprint","IMPRINT",FACE,{"disambiguationData":[TD([[makeQuery(id+"F34.imprint","IMPRINT",EDGE,{"derivedFrom":sQuery(id+"F34.wireOp",EDGE,"E139")}),1.0]])]});
            extrude(context, id + "F35", {"entities" : qUnion([Q0]), "operationType" : NewBodyOperationType.REMOVE, "oppositeDirection" : true, "depth" : 154 * mm, "offsetDistance" : 25 * mm});
        }
        {
            var Q0;
            Q0=makeQuery(id+"F30.boolean.opBoolean","MERGE",FACE,{"derivedFrom":[makeQuery(id+"F25.opExtrude","CAP_FACE",FACE,{"disambiguationData":[OSD([sQuery(id+"F18.wireOp",EDGE,"E102"),sQuery(id+"F24.wireOp",EDGE,"E114"),sQuery(id+"F24.wireOp",EDGE,"E115"),sQuery(id+"F24.wireOp",EDGE,"E116"),sQuery(id+"F24.wireOp",EDGE,"E117"),sQuery(id+"F24.wireOp",EDGE,"E118"),sQuery(id+"F24.wireOp",EDGE,"E119"),sQuery(id+"F24.wireOp",EDGE,"E120"),sQuery(id+"F24.wireOp",EDGE,"E121")])],"isStart":false}),makeQuery(id+"F30.opExtrude","CAP_FACE",FACE,{"disambiguationData":[OSD([sQuery(id+"F29.wireOp",EDGE,"E136")])],"isStart":true})]});
            var sketch = newSketch(context, id + "F36", { "sketchPlane" : qUnion([Q0])});
            skCircle(sketch, "E140", {"center": v(105, 62) * mm, "radius": 31 * mm});
            skSolve(sketch);
        }
        {
            var Q0;
            Q0=makeQuery(id+"F36.imprint","IMPRINT",FACE,{"disambiguationData":[TD([[makeQuery(id+"F36.imprint","IMPRINT",EDGE,{"derivedFrom":sQuery(id+"F36.wireOp",EDGE,"E140")}),1.0]])]});
            var Q1;
            Q1=sQuery(id+"F36.wireOp",EDGE,"E140");
            extrude(context, id + "F37", {"entities" : qUnion([Q0]), "operationType" : NewBodyOperationType.REMOVE, "surfaceEntities" : qUnion([Q1]), "oppositeDirection" : true, "depth" : 22 * mm, "offsetDistance" : 25 * mm});
        }
    });
